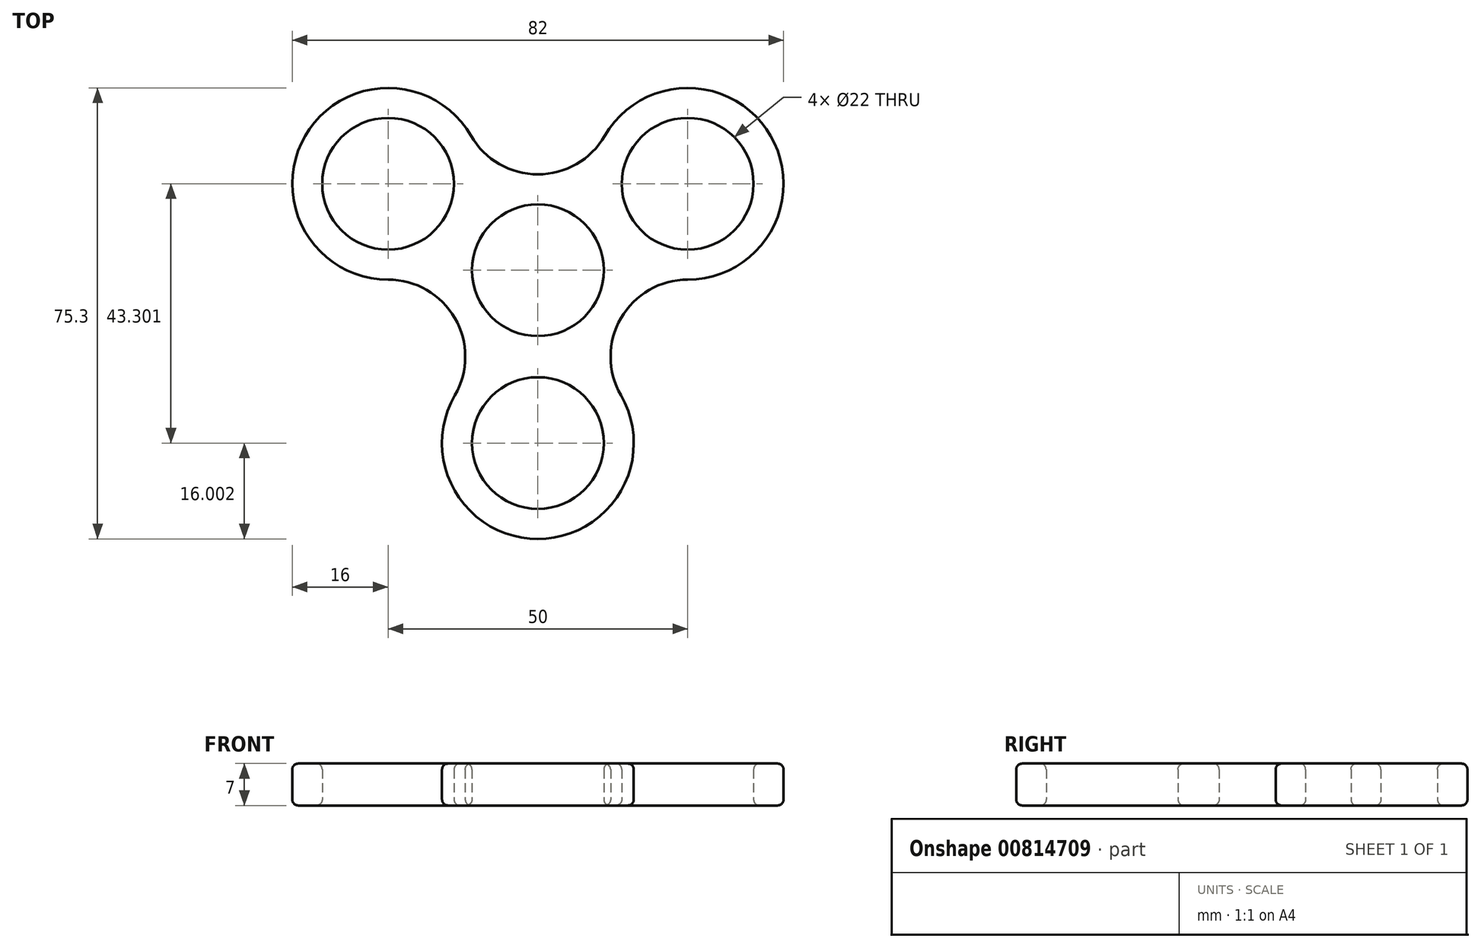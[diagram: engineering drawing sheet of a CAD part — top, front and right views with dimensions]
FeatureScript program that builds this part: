
annotation { "Feature Type Name" : "Feature", "Feature Type Description" : "" }
export const myFeature = defineFeature(function(context is Context, id is Id, definition is map)
    precondition{}
    {
        {
            var Q0;
            Q0=qCreatedBy(makeId("Top.planeOp"),FACE);
            var sketch = newSketch(context, id + "F0", { "sketchPlane" : qUnion([Q0])});
            skCircle(sketch, "E0.cCircle", {"center": v(0, 0) * mm, "radius": 14.43 * mm, "construction": true});
            skLineSegment(sketch, "E0.0", {"start": v(25, 14.43) * mm, "end": v(0, -28.87) * mm, "construction": true});
            skLineSegment(sketch, "E0.1", {"start": v(0, -28.87) * mm, "end": v(-25, 14.43) * mm, "construction": true});
            skLineSegment(sketch, "E0.2", {"start": v(-25, 14.43) * mm, "end": v(25, 14.43) * mm, "construction": true});
            skPoint(sketch, "E0.0.midPoint", {"position": v(12.5, -7.22) * mm});
            skCircle(sketch, "E1", {"center": v(0, 0) * mm, "radius": 11 * mm});
            skCircle(sketch, "E2", {"center": v(25, 14.43) * mm, "radius": 11 * mm});
            skCircle(sketch, "E3", {"center": v(-25, 14.43) * mm, "radius": 11 * mm});
            skCircle(sketch, "E4", {"center": v(0, -28.87) * mm, "radius": 11 * mm});
            skArc(sketch, "E5", {"start": v(-11.14, 22.43) * mm, "mid": v(-38.86, 22.43) * mm, "end": v(-25, -1.57) * mm});
            skArc(sketch, "E6.1.0", {"start": v(-13.86, -20.87) * mm, "mid": v(0, -44.87) * mm, "end": v(13.86, -20.87) * mm});
            skArc(sketch, "E6.2.0", {"start": v(25, -1.57) * mm, "mid": v(38.86, 22.43) * mm, "end": v(11.14, 22.43) * mm});
            skArc(sketch, "E7", {"start": v(-13.86, -20.87) * mm, "mid": v(-13.86, -8) * mm, "end": v(-25, -1.57) * mm});
            skPoint(sketch, "E7.first.point", {"position": v(-25, -1.57) * mm});
            skPoint(sketch, "E7.second.point", {"position": v(-13.86, -20.87) * mm});
            skPoint(sketch, "E7.third.point", {"position": v(-37.46, -17.66) * mm});
            skArc(sketch, "E8.1.0", {"start": v(25, -1.57) * mm, "mid": v(13.86, -8) * mm, "end": v(13.86, -20.87) * mm});
            skArc(sketch, "E8.2.0", {"start": v(-11.14, 22.43) * mm, "mid": v(0, 16) * mm, "end": v(11.14, 22.43) * mm});
            skSolve(sketch);
        }
        {
            var Q0;
            Q0=makeQuery(id+"F0.imprint","IMPRINT",FACE,{"disambiguationData":[TD([[makeQuery(id+"F0.imprint","IMPRINT",EDGE,{"derivedFrom":sQuery(id+"F0.wireOp",EDGE,"E1")}),-1.0]])]});
            extrude(context, id + "F1", {"entities" : qUnion([Q0]), "depth" : 7 * mm, "offsetDistance" : 25 * mm});
        }
        {
            var Q0;
            Q0=makeQuery(id+"F1.opExtrude","CAP_FACE",FACE,{"disambiguationData":[OSD([sQuery(id+"F0.wireOp",EDGE,"E1"),sQuery(id+"F0.wireOp",EDGE,"E2"),sQuery(id+"F0.wireOp",EDGE,"E3"),sQuery(id+"F0.wireOp",EDGE,"E4"),sQuery(id+"F0.wireOp",EDGE,"E5"),sQuery(id+"F0.wireOp",EDGE,"E6.1.0"),sQuery(id+"F0.wireOp",EDGE,"E6.2.0"),sQuery(id+"F0.wireOp",EDGE,"E7"),sQuery(id+"F0.wireOp",EDGE,"E8.1.0"),sQuery(id+"F0.wireOp",EDGE,"E8.2.0")])],"isStart":false});
            var Q1;
            Q1=makeQuery(id+"F1.opExtrude","CAP_FACE",FACE,{"disambiguationData":[OSD([sQuery(id+"F0.wireOp",EDGE,"E1"),sQuery(id+"F0.wireOp",EDGE,"E2"),sQuery(id+"F0.wireOp",EDGE,"E3"),sQuery(id+"F0.wireOp",EDGE,"E4"),sQuery(id+"F0.wireOp",EDGE,"E5"),sQuery(id+"F0.wireOp",EDGE,"E6.1.0"),sQuery(id+"F0.wireOp",EDGE,"E6.2.0"),sQuery(id+"F0.wireOp",EDGE,"E7"),sQuery(id+"F0.wireOp",EDGE,"E8.1.0"),sQuery(id+"F0.wireOp",EDGE,"E8.2.0")])],"isStart":true});
            fillet(context, id + "F2", {"entities" : qUnion([Q0, Q1]), "radius" : 1 * mm, "tangentPropagation" : true, "allowEdgeOverflow" : false});
        }
    });
